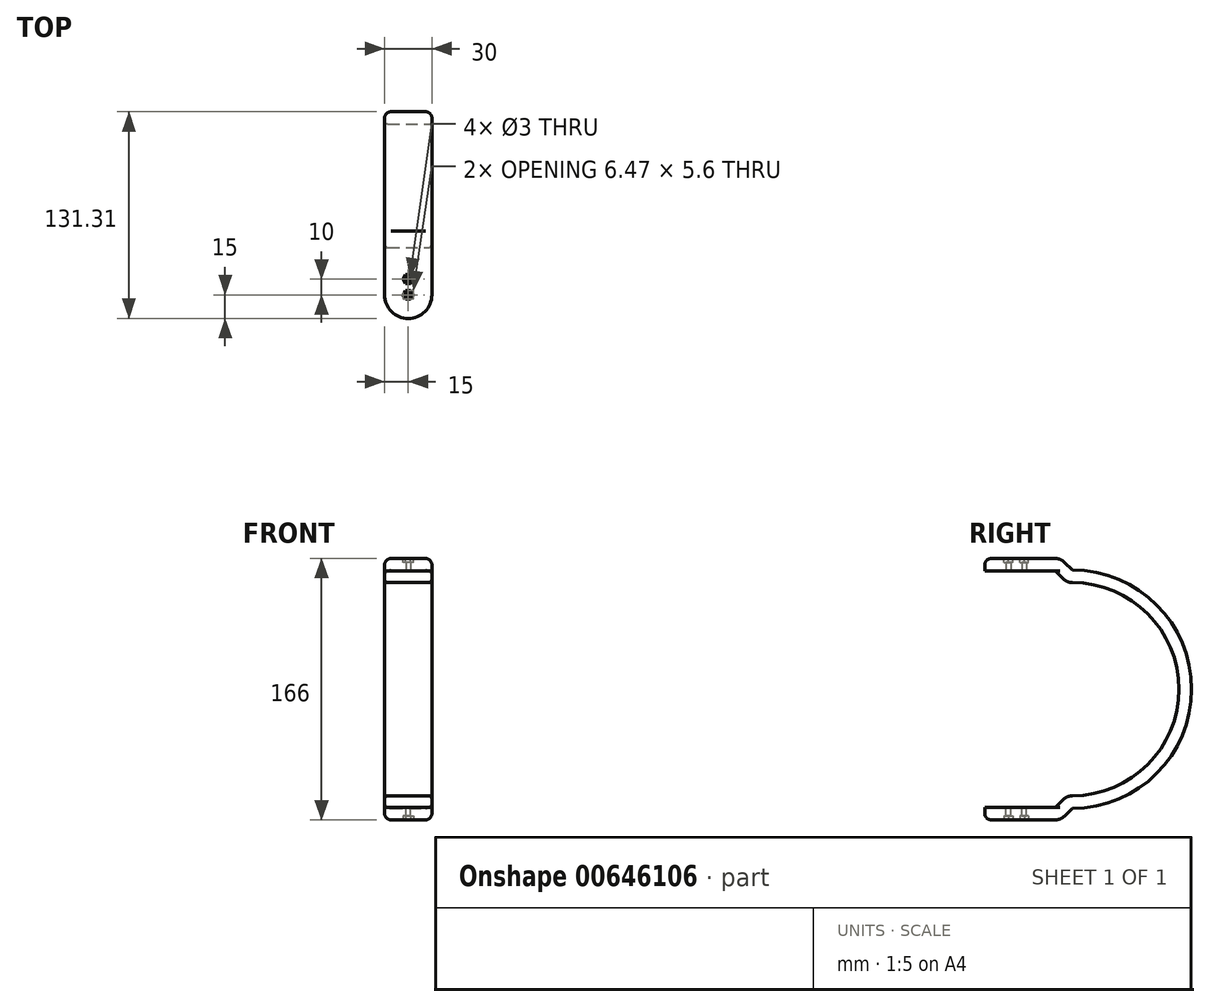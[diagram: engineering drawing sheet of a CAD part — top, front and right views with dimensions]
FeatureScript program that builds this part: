
annotation { "Feature Type Name" : "Feature", "Feature Type Description" : "" }
export const myFeature = defineFeature(function(context is Context, id is Id, definition is map)
    precondition{}
    {
        {
            var Q0;
            Q0=qCreatedBy(makeId("Top.planeOp"),FACE);
            var sketch = newSketch(context, id + "F0", { "sketchPlane" : qUnion([Q0])});
            skCircle(sketch, "E0", {"center": v(0, 0) * mm, "radius": 1.5 * mm});
            skLineSegment(sketch, "E1", {"start": v(-15, -10) * mm, "end": v(-15, 20) * mm});
            skLineSegment(sketch, "E2", {"start": v(15, -10) * mm, "end": v(15, 20) * mm});
            skCircle(sketch, "E3", {"center": v(0, -10) * mm, "radius": 1.5 * mm});
            skLineSegment(sketch, "E4", {"start": v(-15, 20) * mm, "end": v(15, 20) * mm});
            skArc(sketch, "E5", {"start": v(-15, -10) * mm, "mid": v(0, -25) * mm, "end": v(15, -10) * mm});
            skSolve(sketch);
        }
        {
            var Q0;
            Q0=makeQuery(id+"F0.imprint","IMPRINT",FACE,{"disambiguationData":[TD([[makeQuery(id+"F0.imprint","IMPRINT",EDGE,{"derivedFrom":sQuery(id+"F0.wireOp",EDGE,"E1")}),-1.0]])]});
            extrude(context, id + "F1", {"entities" : qUnion([Q0]), "depth" : 8 * mm, "offsetDistance" : 25 * mm});
        }
        {
            var Q0;
            Q0=makeQuery(id+"F1.opExtrude","CAP_EDGE",EDGE,{"disambiguationData":[OSD([sQuery(id+"F0.wireOp",EDGE,"E2")])],"isStart":false});
            fillet(context, id + "F2", {"entities" : qUnion([Q0]), "radius" : 4 * mm, "tangentPropagation" : true, "allowEdgeOverflow" : false});
        }
        {
            var Q0;
            Q0=makeQuery(id+"F1.opExtrude","CAP_FACE",FACE,{"disambiguationData":[OSD([sQuery(id+"F0.wireOp",EDGE,"E0"),sQuery(id+"F0.wireOp",EDGE,"Xe45Hy79-9lb9-8in3-vNjb-7CuShQZwM5bq"),sQuery(id+"F0.wireOp",EDGE,"E1"),sQuery(id+"F0.wireOp",EDGE,"E2"),sQuery(id+"F0.wireOp",EDGE,"E3"),sQuery(id+"F0.wireOp",EDGE,"E4")])],"isStart":false});
            var sketch = newSketch(context, id + "F3", { "sketchPlane" : qUnion([Q0])});
            skCircle(sketch, "E6", {"center": v(0, -10) * mm, "radius": 2.8 * mm});
            skCircle(sketch, "E7", {"center": v(0, 0) * mm, "radius": 2.8 * mm});
            skLineSegment(sketch, "E8.0", {"start": v(-1.62, -7.2) * mm, "end": v(1.62, -7.2) * mm});
            skLineSegment(sketch, "E8.1", {"start": v(1.62, -7.2) * mm, "end": v(3.23, -10) * mm});
            skLineSegment(sketch, "E8.2", {"start": v(3.23, -10) * mm, "end": v(1.62, -12.8) * mm});
            skLineSegment(sketch, "E8.3", {"start": v(1.62, -12.8) * mm, "end": v(-1.62, -12.8) * mm});
            skLineSegment(sketch, "E8.4", {"start": v(-1.62, -12.8) * mm, "end": v(-3.23, -10) * mm});
            skLineSegment(sketch, "E8.5", {"start": v(-3.23, -10) * mm, "end": v(-1.62, -7.2) * mm});
            skPoint(sketch, "E8.0.midPoint", {"position": v(0, -7.2) * mm});
            skLineSegment(sketch, "E9.0", {"start": v(-1.62, 2.8) * mm, "end": v(1.62, 2.8) * mm});
            skLineSegment(sketch, "E9.1", {"start": v(1.62, 2.8) * mm, "end": v(3.23, 0) * mm});
            skLineSegment(sketch, "E9.2", {"start": v(3.23, 0) * mm, "end": v(1.62, -2.8) * mm});
            skLineSegment(sketch, "E9.3", {"start": v(1.62, -2.8) * mm, "end": v(-1.62, -2.8) * mm});
            skLineSegment(sketch, "E9.4", {"start": v(-1.62, -2.8) * mm, "end": v(-3.23, 0) * mm});
            skLineSegment(sketch, "E9.5", {"start": v(-3.23, 0) * mm, "end": v(-1.62, 2.8) * mm});
            skPoint(sketch, "E9.0.midPoint", {"position": v(0, 2.8) * mm});
            skSolve(sketch);
        }
        {
            var Q0;
            Q0 = qSketchRegion(id + "F3", true);
            extrude(context, id + "F4", {"entities" : qUnion([Q0]), "operationType" : NewBodyOperationType.REMOVE, "oppositeDirection" : true, "depth" : 2.5 * mm, "offsetDistance" : 25 * mm});
        }
        {
            var Q0;
            Q0=makeQuery(id+"F1.opExtrude","SWEPT_FACE",FACE,{"disambiguationData":[OSD([sQuery(id+"F0.wireOp",EDGE,"E4")])]});
            var Q1;
            Q1=makeQuery(id+"F1.opExtrude","CAP_EDGE",EDGE,{"disambiguationData":[OSD([sQuery(id+"F0.wireOp",EDGE,"E4")])],"isStart":true});
            revolve(context, id + "F5", {"operationType" : NewBodyOperationType.ADD, "entities" : qUnion([Q0]), "axis" : qUnion([Q1]), "revolveType" : RevolveType.ONE_DIRECTION, "oppositeDirection" : true, "angle" : 45 * degree});
        }
        {
            var Q0;
            Q0=makeQuery(id+"F5.opRevolve","CAP_FACE",FACE,{"disambiguationData":[OSD([sQuery(id+"F0.wireOp",EDGE,"E4")])],"isStart":false});
            extrude(context, id + "F6", {"entities" : qUnion([Q0]), "operationType" : NewBodyOperationType.ADD, "depth" : 7 * mm, "offsetDistance" : 25 * mm});
        }
        {
            var Q0;
            {var subQ0=sQuery(id+"F0.wireOp",EDGE,"E4");var subQ1=sQuery(id+"F0.wireOp",EDGE,"E2");var subQ2=makeQuery(id+"F1.opExtrude","CAP_VERTEX",VERTEX,{"disambiguationData":[OSD([subQ1,subQ0])],"isStart":true});Q0=makeQuery(id+"F6.opExtrude","SWEPT_EDGE",EDGE,{"disambiguationData":[OSD([subQ1,subQ0]),TDD([makeQuery(id+"F5.boolean.opBoolean","MERGE",VERTEX,{"derivedFrom":[subQ2,makeQuery(id+"F5.opRevolve","CAP_VERTEX",VERTEX,{"disambiguationData":[OSD([subQ1,subQ0]),TDD([subQ2])],"isStart":true})]})])]});}
            var Q1;
            {var subQ0=sQuery(id+"F0.wireOp",EDGE,"E4");var subQ1=sQuery(id+"F0.wireOp",EDGE,"E1");var subQ2=makeQuery(id+"F1.opExtrude","CAP_VERTEX",VERTEX,{"disambiguationData":[OSD([subQ1,subQ0])],"isStart":true});Q1=makeQuery(id+"F6.opExtrude","SWEPT_EDGE",EDGE,{"disambiguationData":[OSD([subQ1,subQ0]),TDD([makeQuery(id+"F5.boolean.opBoolean","MERGE",VERTEX,{"derivedFrom":[subQ2,makeQuery(id+"F5.opRevolve","CAP_VERTEX",VERTEX,{"disambiguationData":[OSD([subQ1,subQ0]),TDD([subQ2])],"isStart":true})]})])]});}
            fillet(context, id + "F7", {"entities" : qUnion([Q0, Q1]), "radius" : 2 * mm, "tangentPropagation" : true, "allowEdgeOverflow" : false});
        }
        {
            var Q0;
            Q0=makeQuery(id+"F6.opExtrude","CAP_FACE",FACE,{"disambiguationData":[OSD([sQuery(id+"F0.wireOp",EDGE,"E4")])],"isStart":false});
            var Q1;
            {var subQ0=sQuery(id+"F0.wireOp",EDGE,"E4");Q1=makeQuery(id+"F6.opExtrude","CAP_EDGE",EDGE,{"disambiguationData":[OSD([subQ0]),TDD([makeQuery(id+"F5.opRevolve","CAP_EDGE",EDGE,{"disambiguationData":[OSD([subQ0])],"isStart":false})])],"isStart":false});}
            revolve(context, id + "F8", {"operationType" : NewBodyOperationType.ADD, "entities" : qUnion([Q0]), "axis" : qUnion([Q1]), "revolveType" : RevolveType.ONE_DIRECTION, "angle" : 45 * degree});
        }
        {
            var Q0;
            Q0=qCreatedBy(makeId("Front.planeOp"),FACE);
            cPlane(context, id + "F9", {"entities" : qUnion([Q0]), "cplaneType" : CPlaneType.OFFSET, "offset" : 30.6 * mm, "oppositeDirection" : true, "width" : 150 * mm, "height" : 150 * mm});
        }
        {
            var Q0;
            Q0=qCreatedBy(id+"F9.planeOp",FACE);
            var sketch = newSketch(context, id + "F10", { "sketchPlane" : qUnion([Q0])});
            skLineSegment(sketch, "E10", {"start": v(27.59, -75) * mm, "end": v(-33.75, -75) * mm});
            skSolve(sketch);
        }
        {
            var Q0;
            Q0=makeQuery(id+"F8.opRevolve","CAP_FACE",FACE,{"disambiguationData":[OSD([sQuery(id+"F0.wireOp",EDGE,"E4")])],"isStart":false});
            var Q1;
            Q1=sQuery(id+"F10.wireOp",EDGE,"E10");
            revolve(context, id + "F11", {"operationType" : NewBodyOperationType.ADD, "entities" : qUnion([Q0]), "axis" : qUnion([Q1]), "revolveType" : RevolveType.ONE_DIRECTION, "angle" : 180 * degree});
        }
        {
            var Q0;
            Q0=qCreatedBy(makeId("Top.planeOp"),FACE);
            cPlane(context, id + "F12", {"entities" : qUnion([Q0]), "cplaneType" : CPlaneType.OFFSET, "offset" : 75 * mm, "oppositeDirection" : true, "width" : 150 * mm, "height" : 150 * mm});
        }
        {
            var Q0;
            Q0=makeQuery(id+"F1.opExtrude","SWEPT_BODY",BODY,{"disambiguationData":[OSD([sQuery(id+"F0.wireOp",EDGE,"E0"),sQuery(id+"F0.wireOp",EDGE,"E1"),sQuery(id+"F0.wireOp",EDGE,"E2"),sQuery(id+"F0.wireOp",EDGE,"E3"),sQuery(id+"F0.wireOp",EDGE,"E4"),sQuery(id+"F0.wireOp",EDGE,"E5")])]});
            var Q1;
            Q1=qCreatedBy(id+"F12.planeOp",FACE);
            mirror(context, id + "F13", {"operationType" : NewBodyOperationType.ADD, "entities" : qUnion([Q0]), "mirrorPlane" : qUnion([Q1])});
        }
    });
